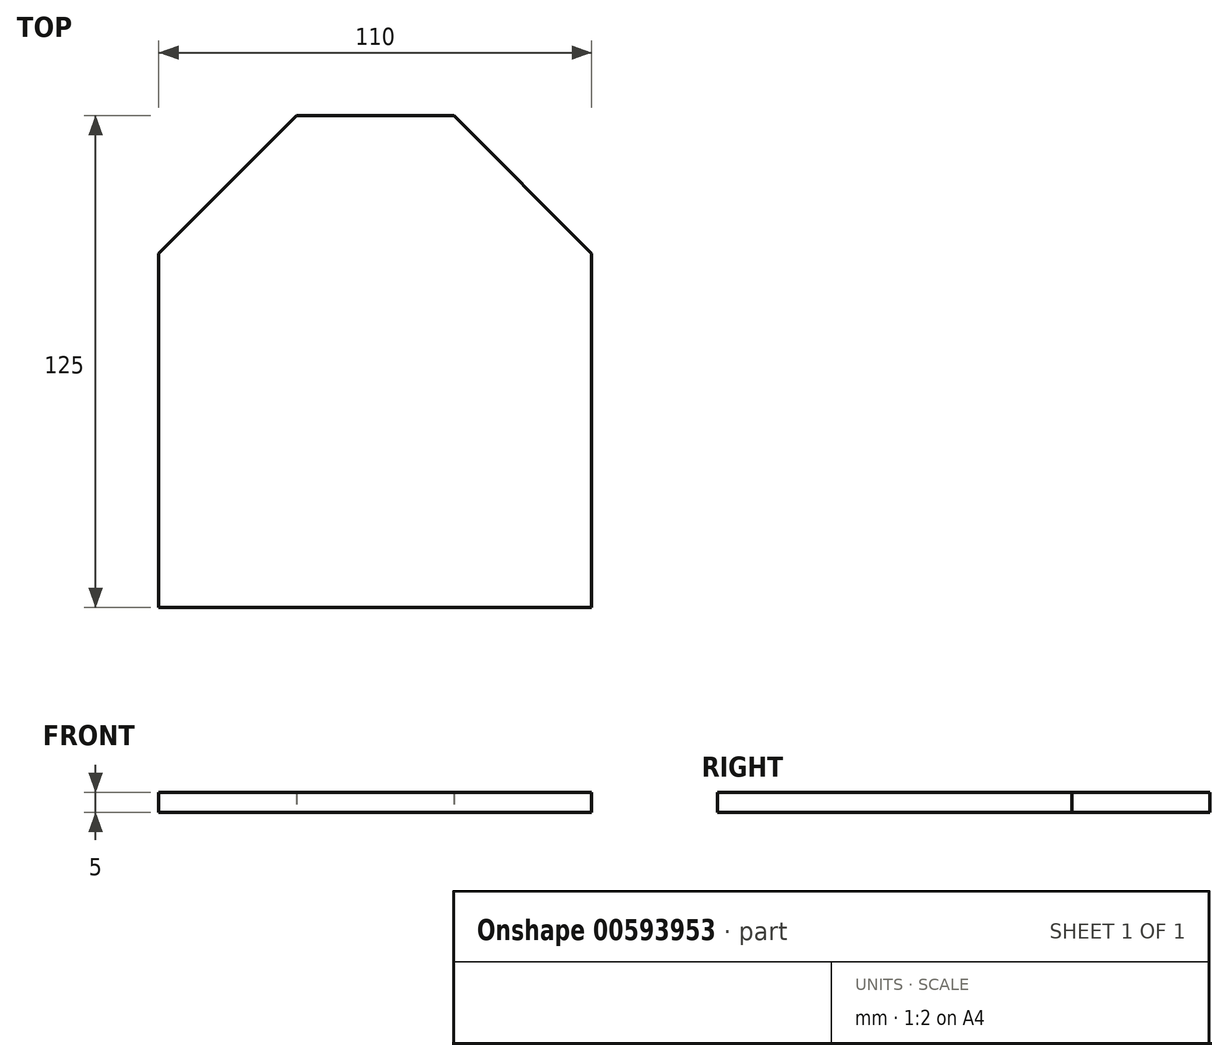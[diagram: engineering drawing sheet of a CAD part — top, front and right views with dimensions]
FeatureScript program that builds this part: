
annotation { "Feature Type Name" : "Feature", "Feature Type Description" : "" }
export const myFeature = defineFeature(function(context is Context, id is Id, definition is map)
    precondition{}
    {
        {
            var Q0;
            Q0=qCreatedBy(makeId("Top.planeOp"),FACE);
            var sketch = newSketch(context, id + "F0", { "sketchPlane" : qUnion([Q0])});
            skLineSegment(sketch, "E0", {"start": v(0, 62.5) * mm, "end": v(0, -62.5) * mm, "construction": true});
            skLineSegment(sketch, "E1", {"start": v(-55, 0) * mm, "end": v(55, 0) * mm, "construction": true});
            skLineSegment(sketch, "E2.bottom", {"start": v(-20, 62.5) * mm, "end": v(20, 62.5) * mm});
            skLineSegment(sketch, "E2.top", {"start": v(-55, -62.5) * mm, "end": v(55, -62.5) * mm});
            skLineSegment(sketch, "E2.left", {"start": v(-55, 27.5) * mm, "end": v(-55, -62.5) * mm});
            skLineSegment(sketch, "E2.right", {"start": v(55, 62.5) * mm, "end": v(55, -62.5) * mm});
            skLineSegment(sketch, "E3", {"start": v(-55, 27.5) * mm, "end": v(-20, 62.5) * mm});
            skLineSegment(sketch, "E4.MirrorCS", {"start": v(55, 27.5) * mm, "end": v(20, 62.5) * mm});
            skPoint(sketch, "E5.orphan", {"position": v(-55, 62.5) * mm});
            skSolve(sketch);
        }
        {
            var Q0;
            Q0=makeQuery(id+"F0.imprint","IMPRINT",FACE,{"disambiguationData":[TD([[makeQuery(id+"F0.imprint","IMPRINT",EDGE,{"derivedFrom":sQuery(id+"F0.wireOp",EDGE,"E2.bottom")}),-1.0]])]});
            extrude(context, id + "F1", {"entities" : qUnion([Q0]), "endBound" : BoundingType.SYMMETRIC, "depth" : 5 * mm, "offsetDistance" : 25 * mm});
        }
    });
